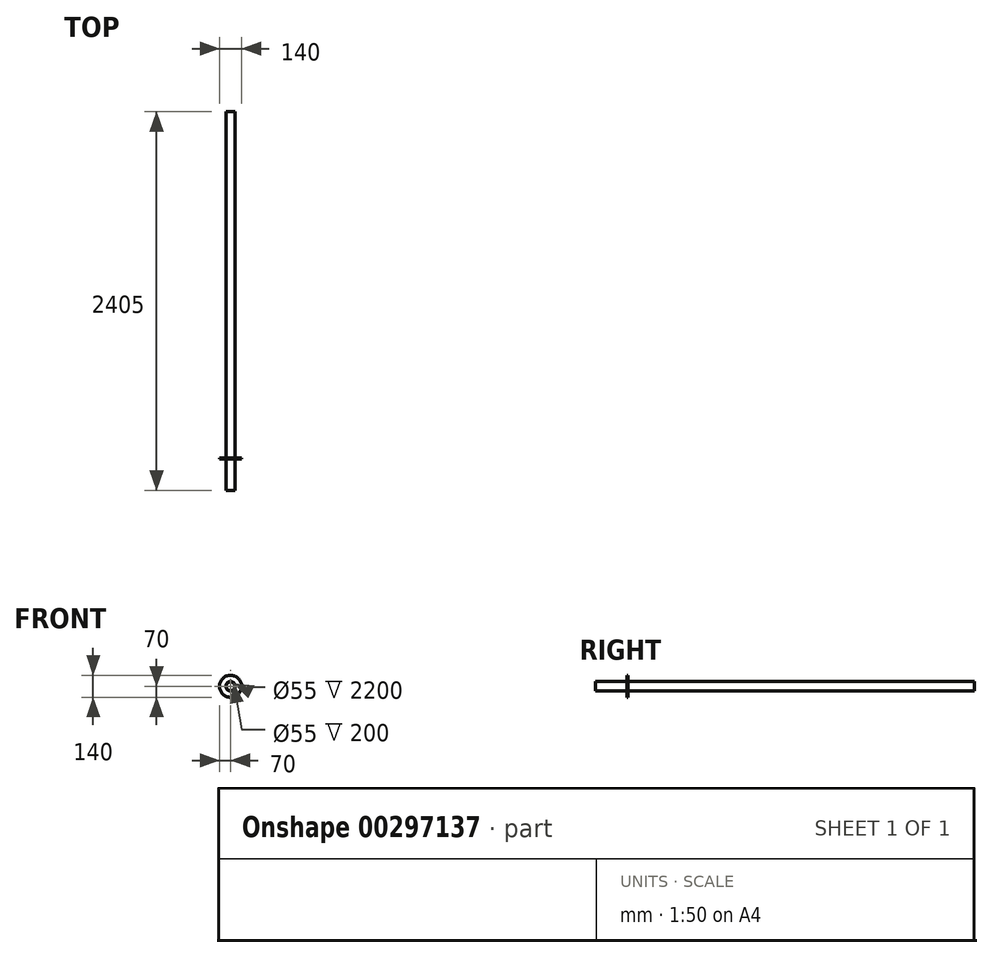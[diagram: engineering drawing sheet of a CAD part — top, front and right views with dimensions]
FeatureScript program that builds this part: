
annotation { "Feature Type Name" : "Feature", "Feature Type Description" : "" }
export const myFeature = defineFeature(function(context is Context, id is Id, definition is map)
    precondition{}
    {
        {
            var Q0;
            Q0=qCreatedBy(makeId("Front.planeOp"),FACE);
            var sketch = newSketch(context, id + "F0", { "sketchPlane" : qUnion([Q0])});
            skCircle(sketch, "E0", {"center": v(0, 0) * mm, "radius": 30 * mm});
            skCircle(sketch, "E1", {"center": v(0, 0) * mm, "radius": 27.5 * mm});
            skSolve(sketch);
        }
        {
            var Q0;
            Q0=makeQuery(id+"F0.imprint","IMPRINT",FACE,{"disambiguationData":[TD([[makeQuery(id+"F0.imprint","IMPRINT",EDGE,{"derivedFrom":sQuery(id+"F0.wireOp",EDGE,"E0")}),1.0]])]});
            extrude(context, id + "F1", {"entities" : qUnion([Q0]), "endBound" : BoundingType.SYMMETRIC, "depth" : 2200 * mm});
        }
        {
            var Q0;
            Q0=makeQuery(id+"F1.opExtrude","CAP_FACE",FACE,{"disambiguationData":[OSD([sQuery(id+"F0.wireOp",EDGE,"E0"),sQuery(id+"F0.wireOp",EDGE,"E1")])],"isStart":false});
            var sketch = newSketch(context, id + "F2", { "sketchPlane" : qUnion([Q0])});
            skCircle(sketch, "E2", {"center": v(0, 0) * mm, "radius": 70 * mm});
            skSolve(sketch);
        }
        {
            var Q0;
            Q0 = qSketchRegion(id + "F2", true);
            extrude(context, id + "F3", {"entities" : qUnion([Q0]), "operationType" : NewBodyOperationType.ADD, "depth" : 5 * mm});
        }
        {
            var Q0;
            Q0=makeQuery(id+"F3.opExtrude","CAP_FACE",FACE,{"disambiguationData":[OSD([sQuery(id+"F2.wireOp",EDGE,"E2")])],"isStart":false});
            var sketch = newSketch(context, id + "F4", { "sketchPlane" : qUnion([Q0])});
            skCircle(sketch, "E3", {"center": v(0, 0) * mm, "radius": 30 * mm});
            skCircle(sketch, "E4", {"center": v(0, 0) * mm, "radius": 27.5 * mm});
            skSolve(sketch);
        }
        {
            var Q0;
            Q0=makeQuery(id+"F4.imprint","IMPRINT",FACE,{"disambiguationData":[TD([[makeQuery(id+"F4.imprint","IMPRINT",EDGE,{"derivedFrom":sQuery(id+"F4.wireOp",EDGE,"E3")}),1.0]])]});
            var Q1;
            Q1=sQuery(id+"F4.wireOp",EDGE,"E3");
            var Q2;
            Q2=sQuery(id+"F4.wireOp",EDGE,"E4");
            extrude(context, id + "F5", {"entities" : qUnion([Q0]), "operationType" : NewBodyOperationType.ADD, "surfaceEntities" : qUnion([Q1, Q2]), "depth" : 200 * mm});
        }
    });
